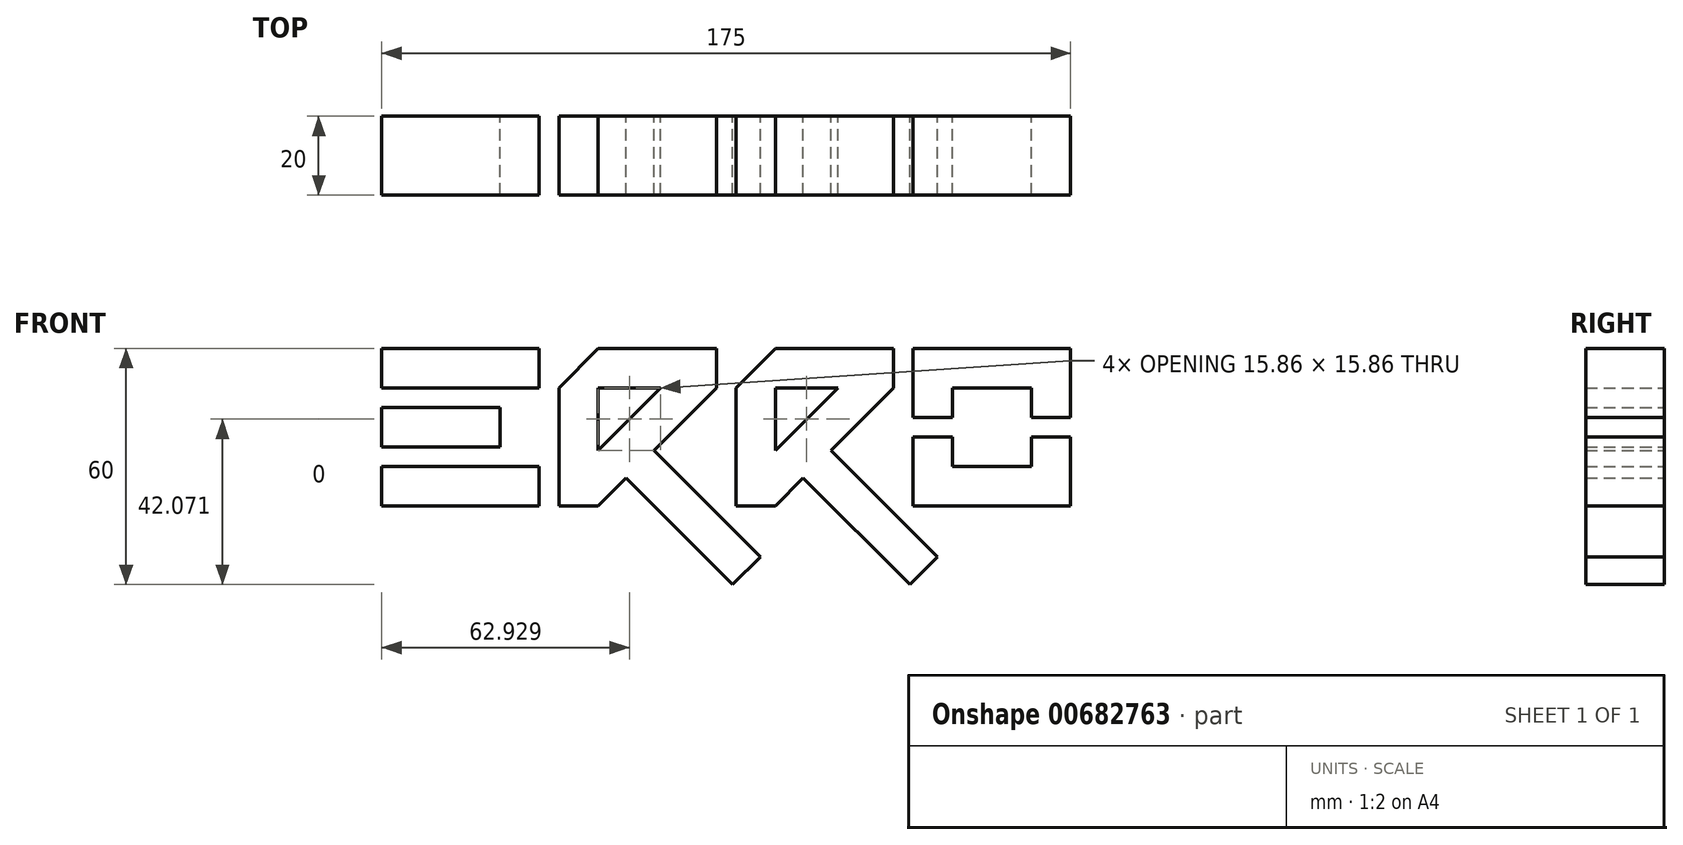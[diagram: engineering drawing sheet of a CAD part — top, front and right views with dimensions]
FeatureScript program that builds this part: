
annotation { "Feature Type Name" : "Feature", "Feature Type Description" : "" }
export const myFeature = defineFeature(function(context is Context, id is Id, definition is map)
    precondition{}
    {
        {
            var Q0;
            Q0=qCreatedBy(makeId("Front.planeOp"),FACE);
            var sketch = newSketch(context, id + "F0", { "sketchPlane" : qUnion([Q0])});
            skLineSegment(sketch, "E0.bottom", {"start": v(0, 0) * mm, "end": v(-40, 0) * mm});
            skLineSegment(sketch, "E0.top", {"start": v(0, 10) * mm, "end": v(-40, 10) * mm});
            skLineSegment(sketch, "E0.left", {"start": v(0, 0) * mm, "end": v(0, 10) * mm});
            skLineSegment(sketch, "E0.right", {"start": v(-40, 0) * mm, "end": v(-40, 10) * mm});
            skLineSegment(sketch, "E1.bottom", {"start": v(-40, 25) * mm, "end": v(-10, 25) * mm});
            skLineSegment(sketch, "E1.top", {"start": v(-40, 15) * mm, "end": v(-10, 15) * mm});
            skLineSegment(sketch, "E1.left", {"start": v(-40, 25) * mm, "end": v(-40, 15) * mm});
            skLineSegment(sketch, "E1.right", {"start": v(-10, 25) * mm, "end": v(-10, 15) * mm});
            skLineSegment(sketch, "E2.bottom", {"start": v(-40, 30) * mm, "end": v(0, 30) * mm});
            skLineSegment(sketch, "E2.top", {"start": v(-40, 40) * mm, "end": v(0, 40) * mm});
            skLineSegment(sketch, "E2.left", {"start": v(-40, 30) * mm, "end": v(-40, 40) * mm});
            skLineSegment(sketch, "E2.right", {"start": v(0, 30) * mm, "end": v(0, 40) * mm});
            skLineSegment(sketch, "E3", {"start": v(5, 0) * mm, "end": v(5, 30) * mm});
            skLineSegment(sketch, "E4", {"start": v(15, 40) * mm, "end": v(45, 40) * mm});
            skLineSegment(sketch, "E5", {"start": v(45, 40) * mm, "end": v(45, 30) * mm});
            skLineSegment(sketch, "E6", {"start": v(15, 0) * mm, "end": v(5, 0) * mm});
            skLineSegment(sketch, "E7", {"start": v(45, 30) * mm, "end": v(29.14, 14.14) * mm});
            skLineSegment(sketch, "E8", {"start": v(15, 0) * mm, "end": v(15, 0) * mm});
            skLineSegment(sketch, "E9", {"start": v(15, 30) * mm, "end": v(30.86, 30) * mm});
            skLineSegment(sketch, "E10", {"start": v(30.86, 30) * mm, "end": v(15, 14.14) * mm});
            skLineSegment(sketch, "E11", {"start": v(15, 14.14) * mm, "end": v(15, 30) * mm});
            skLineSegment(sketch, "E12", {"start": v(22.07, 7.07) * mm, "end": v(49.14, -20) * mm});
            skLineSegment(sketch, "E13", {"start": v(56.21, -12.93) * mm, "end": v(29.14, 14.14) * mm});
            skLineSegment(sketch, "E14", {"start": v(15, 14.14) * mm, "end": v(22.07, 7.07) * mm, "construction": true});
            skLineSegment(sketch, "E15.trimOffspring", {"start": v(22.07, 7.07) * mm, "end": v(15, 0) * mm});
            skLineSegment(sketch, "E16", {"start": v(50, 0) * mm, "end": v(50, 30) * mm});
            skLineSegment(sketch, "E17", {"start": v(60, 40) * mm, "end": v(90, 40) * mm});
            skLineSegment(sketch, "E18", {"start": v(90, 40) * mm, "end": v(90, 30) * mm});
            skLineSegment(sketch, "E19", {"start": v(60, 0) * mm, "end": v(50, 0) * mm});
            skLineSegment(sketch, "E20", {"start": v(90, 30) * mm, "end": v(74.14, 14.14) * mm});
            skLineSegment(sketch, "E21", {"start": v(60, 30) * mm, "end": v(75.86, 30) * mm});
            skLineSegment(sketch, "E22", {"start": v(75.86, 30) * mm, "end": v(60, 14.14) * mm});
            skLineSegment(sketch, "E23", {"start": v(60, 14.14) * mm, "end": v(60, 30) * mm});
            skLineSegment(sketch, "E24", {"start": v(67.07, 7.07) * mm, "end": v(94.14, -20) * mm});
            skLineSegment(sketch, "E25", {"start": v(101.21, -12.93) * mm, "end": v(74.14, 14.14) * mm});
            skLineSegment(sketch, "E26", {"start": v(60, 14.14) * mm, "end": v(67.07, 7.07) * mm, "construction": true});
            skLineSegment(sketch, "E27.trimOffspring", {"start": v(67.07, 7.07) * mm, "end": v(60, 0) * mm});
            skLineSegment(sketch, "E28.bottom", {"start": v(95, 0) * mm, "end": v(135, 0) * mm});
            skLineSegment(sketch, "E28.top", {"start": v(95, 40) * mm, "end": v(135, 40) * mm});
            skLineSegment(sketch, "E28.left", {"start": v(95, 0) * mm, "end": v(95, 17.5) * mm});
            skLineSegment(sketch, "E28.right", {"start": v(135, 0) * mm, "end": v(135, 17.5) * mm});
            skLineSegment(sketch, "E29.bottom", {"start": v(105, 30) * mm, "end": v(125, 30) * mm});
            skLineSegment(sketch, "E29.top", {"start": v(105, 10) * mm, "end": v(125, 10) * mm});
            skLineSegment(sketch, "E29.left", {"start": v(105, 30) * mm, "end": v(105, 22.5) * mm});
            skLineSegment(sketch, "E29.right", {"start": v(125, 30) * mm, "end": v(125, 22.5) * mm});
            skLineSegment(sketch, "E30", {"start": v(95, 17.5) * mm, "end": v(105, 17.5) * mm});
            skLineSegment(sketch, "E31", {"start": v(105, 22.5) * mm, "end": v(95, 22.5) * mm});
            skLineSegment(sketch, "E32", {"start": v(125, 22.5) * mm, "end": v(135, 22.5) * mm});
            skLineSegment(sketch, "E33", {"start": v(125, 17.5) * mm, "end": v(135, 17.5) * mm});
            skLineSegment(sketch, "E34.trimOffspring", {"start": v(95, 22.5) * mm, "end": v(95, 40) * mm});
            skLineSegment(sketch, "E35.trimOffspring", {"start": v(105, 17.5) * mm, "end": v(105, 10) * mm});
            skLineSegment(sketch, "E36.trimOffspring", {"start": v(125, 17.5) * mm, "end": v(125, 10) * mm});
            skLineSegment(sketch, "E37.trimOffspring", {"start": v(135, 22.5) * mm, "end": v(135, 40) * mm});
            skLineSegment(sketch, "E38", {"start": v(49.14, -20) * mm, "end": v(56.21, -12.93) * mm});
            skLineSegment(sketch, "E39", {"start": v(94.14, -20) * mm, "end": v(101.21, -12.93) * mm});
            skLineSegment(sketch, "E40", {"start": v(5, 30) * mm, "end": v(15, 40) * mm});
            skLineSegment(sketch, "E41", {"start": v(50, 30) * mm, "end": v(60, 40) * mm});
            skSolve(sketch);
        }
        {
            var Q0;
            Q0=makeQuery(id+"F0.imprint","IMPRINT",FACE,{"disambiguationData":[TD([[makeQuery(id+"F0.imprint","IMPRINT",EDGE,{"derivedFrom":sQuery(id+"F0.wireOp",EDGE,"E2.bottom")}),1.0]])]});
            var Q1;
            Q1=makeQuery(id+"F0.imprint","IMPRINT",FACE,{"disambiguationData":[TD([[makeQuery(id+"F0.imprint","IMPRINT",EDGE,{"derivedFrom":sQuery(id+"F0.wireOp",EDGE,"E1.bottom")}),-1.0]])]});
            var Q2;
            Q2=makeQuery(id+"F0.imprint","IMPRINT",FACE,{"disambiguationData":[TD([[makeQuery(id+"F0.imprint","IMPRINT",EDGE,{"derivedFrom":sQuery(id+"F0.wireOp",EDGE,"E0.bottom")}),-1.0]])]});
            var Q3;
            Q3=makeQuery(id+"F0.imprint","IMPRINT",FACE,{"disambiguationData":[TD([[makeQuery(id+"F0.imprint","IMPRINT",EDGE,{"derivedFrom":sQuery(id+"F0.wireOp",EDGE,"E3")}),-1.0]])]});
            var Q4;
            {var subQ3=sQuery(id+"F0.wireOp",EDGE,"E17");Q4=makeQuery(id+"F0.imprint","IMPRINT",FACE,{"disambiguationData":[TD([[makeQuery(id+"F0.imprint","IMPRINT",EDGE,{"derivedFrom":subQ3}),-1.0]])]});}
            var Q5;
            Q5=makeQuery(id+"F0.imprint","IMPRINT",FACE,{"disambiguationData":[TD([[makeQuery(id+"F0.imprint","IMPRINT",EDGE,{"derivedFrom":sQuery(id+"F0.wireOp",EDGE,"E28.bottom")}),1.0]])]});
            var Q6;
            Q6=makeQuery(id+"F0.imprint","IMPRINT",FACE,{"disambiguationData":[TD([[makeQuery(id+"F0.imprint","IMPRINT",EDGE,{"derivedFrom":sQuery(id+"F0.wireOp",EDGE,"E28.top")}),-1.0]])]});
            extrude(context, id + "F1", {"entities" : qUnion([Q0, Q1, Q2, Q3, Q4, Q5, Q6]), "depth" : 20 * mm, "offsetDistance" : 25 * mm});
        }
    });
